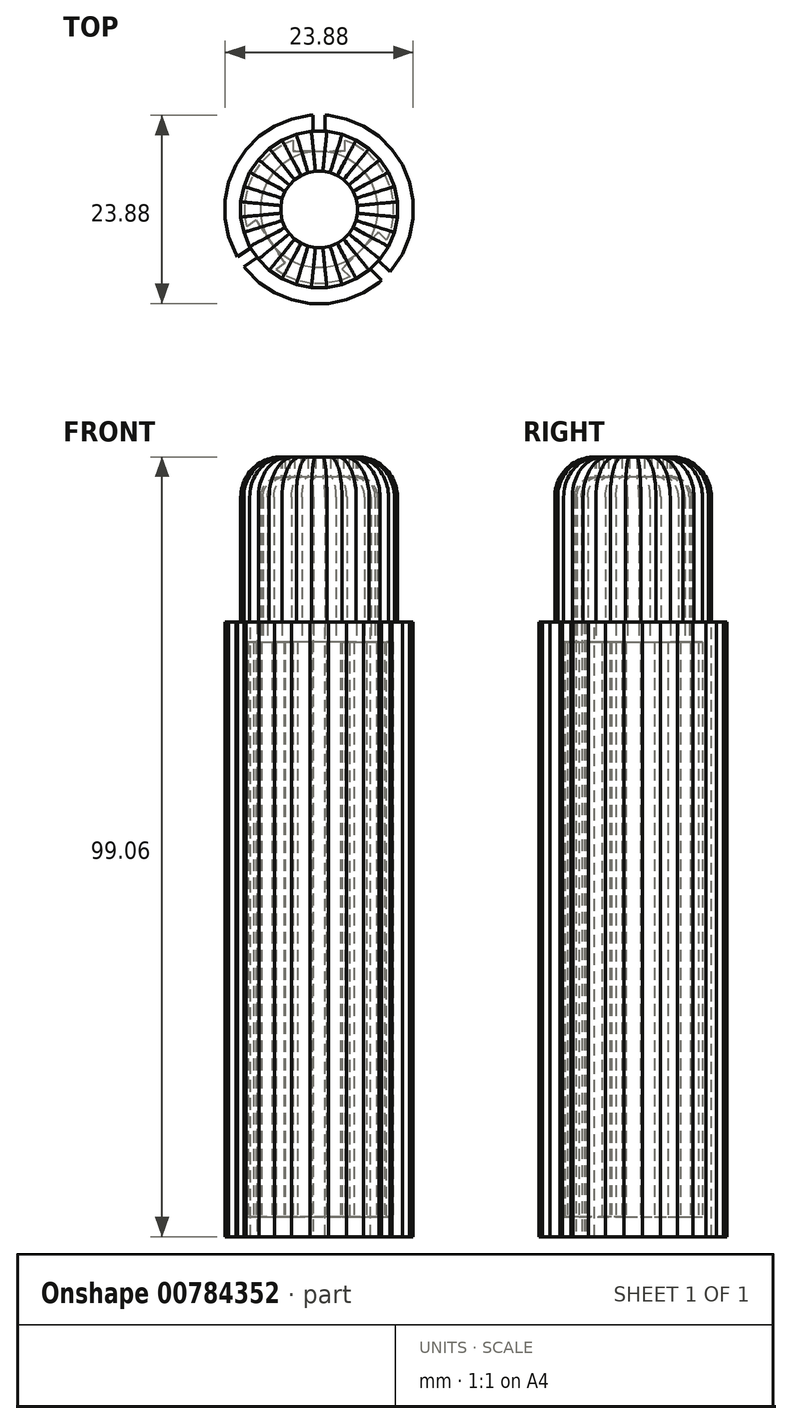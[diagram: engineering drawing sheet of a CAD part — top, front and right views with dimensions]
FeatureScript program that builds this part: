
annotation { "Feature Type Name" : "Feature", "Feature Type Description" : "" }
export const myFeature = defineFeature(function(context is Context, id is Id, definition is map)
    precondition{}
    {
        {
            var Q0;
            Q0=qCreatedBy(makeId("Top.planeOp"),FACE);
            var sketch = newSketch(context, id + "F0", { "sketchPlane" : qUnion([Q0])});
            skCircle(sketch, "E0.cCircle", {"center": v(0, 0) * mm, "radius": 9.95 * mm, "construction": true});
            skLineSegment(sketch, "E0.0", {"start": v(-0.98, 9.95) * mm, "end": v(-0.67, 9.95) * mm});
            skLineSegment(sketch, "E0.1", {"start": v(0.98, 9.95) * mm, "end": v(2.9, 9.57) * mm});
            skLineSegment(sketch, "E0.2", {"start": v(2.9, 9.57) * mm, "end": v(4.71, 8.82) * mm});
            skLineSegment(sketch, "E0.3", {"start": v(4.71, 8.82) * mm, "end": v(6.34, 7.73) * mm});
            skLineSegment(sketch, "E0.4", {"start": v(6.34, 7.73) * mm, "end": v(7.73, 6.34) * mm});
            skLineSegment(sketch, "E0.5", {"start": v(7.73, 6.34) * mm, "end": v(8.82, 4.71) * mm});
            skLineSegment(sketch, "E0.6", {"start": v(8.82, 4.71) * mm, "end": v(9.57, 2.9) * mm});
            skLineSegment(sketch, "E0.7", {"start": v(9.57, 2.9) * mm, "end": v(9.95, 0.98) * mm});
            skLineSegment(sketch, "E0.8", {"start": v(9.95, 0.98) * mm, "end": v(9.95, -0.98) * mm});
            skLineSegment(sketch, "E0.9", {"start": v(9.95, -0.98) * mm, "end": v(9.57, -2.9) * mm});
            skLineSegment(sketch, "E0.10", {"start": v(9.57, -2.9) * mm, "end": v(8.82, -4.71) * mm});
            skLineSegment(sketch, "E0.11", {"start": v(8.82, -4.71) * mm, "end": v(7.73, -6.34) * mm});
            skLineSegment(sketch, "E0.12", {"start": v(7.73, -6.34) * mm, "end": v(6.34, -7.73) * mm});
            skLineSegment(sketch, "E0.13", {"start": v(6.34, -7.73) * mm, "end": v(6.15, -7.86) * mm});
            skLineSegment(sketch, "E0.14", {"start": v(4.71, -8.82) * mm, "end": v(2.9, -9.57) * mm});
            skLineSegment(sketch, "E0.15", {"start": v(2.9, -9.57) * mm, "end": v(0.98, -9.95) * mm});
            skLineSegment(sketch, "E0.16", {"start": v(0.98, -9.95) * mm, "end": v(-0.98, -9.95) * mm});
            skLineSegment(sketch, "E0.17", {"start": v(-0.98, -9.95) * mm, "end": v(-2.9, -9.57) * mm});
            skLineSegment(sketch, "E0.18", {"start": v(-2.9, -9.57) * mm, "end": v(-4.71, -8.82) * mm});
            skLineSegment(sketch, "E0.19", {"start": v(-4.71, -8.82) * mm, "end": v(-6.34, -7.73) * mm});
            skLineSegment(sketch, "E0.20", {"start": v(-6.34, -7.73) * mm, "end": v(-7.73, -6.34) * mm});
            skLineSegment(sketch, "E0.21", {"start": v(-7.73, -6.34) * mm, "end": v(-7.86, -6.15) * mm});
            skLineSegment(sketch, "E0.22", {"start": v(-8.82, -4.71) * mm, "end": v(-9.57, -2.9) * mm});
            skLineSegment(sketch, "E0.23", {"start": v(-9.57, -2.9) * mm, "end": v(-9.95, -0.98) * mm});
            skLineSegment(sketch, "E0.24", {"start": v(-9.95, -0.98) * mm, "end": v(-9.95, 0.98) * mm});
            skLineSegment(sketch, "E0.25", {"start": v(-9.95, 0.98) * mm, "end": v(-9.57, 2.9) * mm});
            skLineSegment(sketch, "E0.26", {"start": v(-9.57, 2.9) * mm, "end": v(-8.82, 4.71) * mm});
            skLineSegment(sketch, "E0.27", {"start": v(-8.82, 4.71) * mm, "end": v(-7.73, 6.34) * mm});
            skLineSegment(sketch, "E0.28", {"start": v(-7.73, 6.34) * mm, "end": v(-6.34, 7.73) * mm});
            skLineSegment(sketch, "E0.29", {"start": v(-6.34, 7.73) * mm, "end": v(-4.71, 8.82) * mm});
            skLineSegment(sketch, "E0.30", {"start": v(-4.71, 8.82) * mm, "end": v(-2.9, 9.57) * mm});
            skLineSegment(sketch, "E0.31", {"start": v(-2.9, 9.57) * mm, "end": v(-0.98, 9.95) * mm});
            skPoint(sketch, "E0.0.midPoint", {"position": v(0, 9.95) * mm});
            skLineSegment(sketch, "E1.trimOffspring", {"start": v(0.82, 9.95) * mm, "end": v(0.98, 9.95) * mm});
            skLineSegment(sketch, "E2.trimOffspring", {"start": v(-8.7, -4.9) * mm, "end": v(-8.82, -4.71) * mm});
            skPoint(sketch, "E3.orphan", {"position": v(-8.27, -5.53) * mm});
            skPoint(sketch, "E4.start.orphan", {"position": v(5.53, -8.27) * mm});
            skLineSegment(sketch, "E5.trimOffspring", {"start": v(4.9, -8.7) * mm, "end": v(4.71, -8.82) * mm});
            skLineSegment(sketch, "E6", {"start": v(-0.67, 9.95) * mm, "end": v(0.82, 9.95) * mm});
            skLineSegment(sketch, "E7", {"start": v(6.15, -7.86) * mm, "end": v(4.9, -8.7) * mm});
            skLineSegment(sketch, "E8", {"start": v(-8.7, -4.9) * mm, "end": v(-7.86, -6.15) * mm});
            skSolve(sketch);
        }
        {
            var Q0;
            Q0=qCreatedBy(makeId("Top.planeOp"),FACE);
            var sketch = newSketch(context, id + "F1", { "sketchPlane" : qUnion([Q0])});
            skCircle(sketch, "E9.cCircle", {"center": v(0, 0) * mm, "radius": 11.94 * mm, "construction": true});
            skLineSegment(sketch, "E9.0", {"start": v(-1.18, 11.94) * mm, "end": v(-0.75, 11.94) * mm});
            skLineSegment(sketch, "E9.1", {"start": v(1.18, 11.94) * mm, "end": v(3.48, 11.48) * mm});
            skLineSegment(sketch, "E9.2", {"start": v(3.48, 11.48) * mm, "end": v(5.66, 10.58) * mm});
            skLineSegment(sketch, "E9.3", {"start": v(5.66, 10.58) * mm, "end": v(7.61, 9.28) * mm});
            skLineSegment(sketch, "E9.4", {"start": v(7.61, 9.28) * mm, "end": v(9.28, 7.61) * mm});
            skLineSegment(sketch, "E9.5", {"start": v(9.28, 7.61) * mm, "end": v(10.58, 5.66) * mm});
            skLineSegment(sketch, "E9.6", {"start": v(10.58, 5.66) * mm, "end": v(11.48, 3.48) * mm});
            skLineSegment(sketch, "E9.7", {"start": v(11.48, 3.48) * mm, "end": v(11.94, 1.18) * mm});
            skLineSegment(sketch, "E9.8", {"start": v(11.94, 1.18) * mm, "end": v(11.94, -1.18) * mm});
            skLineSegment(sketch, "E9.9", {"start": v(11.94, -1.18) * mm, "end": v(11.48, -3.48) * mm});
            skLineSegment(sketch, "E9.10", {"start": v(11.48, -3.48) * mm, "end": v(10.58, -5.66) * mm});
            skLineSegment(sketch, "E9.11", {"start": v(10.58, -5.66) * mm, "end": v(9.28, -7.61) * mm});
            skLineSegment(sketch, "E9.12", {"start": v(9.28, -7.61) * mm, "end": v(8.97, -7.91) * mm});
            skLineSegment(sketch, "E9.13", {"start": v(7.61, -9.28) * mm, "end": v(5.66, -10.58) * mm});
            skLineSegment(sketch, "E9.14", {"start": v(5.66, -10.58) * mm, "end": v(3.48, -11.48) * mm});
            skLineSegment(sketch, "E9.15", {"start": v(3.48, -11.48) * mm, "end": v(1.18, -11.94) * mm});
            skLineSegment(sketch, "E9.16", {"start": v(1.18, -11.94) * mm, "end": v(-1.18, -11.94) * mm});
            skLineSegment(sketch, "E9.17", {"start": v(-1.18, -11.94) * mm, "end": v(-3.48, -11.48) * mm});
            skLineSegment(sketch, "E9.18", {"start": v(-3.48, -11.48) * mm, "end": v(-5.66, -10.58) * mm});
            skLineSegment(sketch, "E9.19", {"start": v(-5.66, -10.58) * mm, "end": v(-7.61, -9.28) * mm});
            skLineSegment(sketch, "E9.20", {"start": v(-7.61, -9.28) * mm, "end": v(-9.28, -7.61) * mm});
            skLineSegment(sketch, "E9.21", {"start": v(-9.28, -7.61) * mm, "end": v(-9.51, -7.26) * mm});
            skLineSegment(sketch, "E9.22", {"start": v(-10.58, -5.66) * mm, "end": v(-11.48, -3.48) * mm});
            skLineSegment(sketch, "E9.23", {"start": v(-11.48, -3.48) * mm, "end": v(-11.94, -1.18) * mm});
            skLineSegment(sketch, "E9.24", {"start": v(-11.94, -1.18) * mm, "end": v(-11.94, 1.18) * mm});
            skLineSegment(sketch, "E9.25", {"start": v(-11.94, 1.18) * mm, "end": v(-11.48, 3.48) * mm});
            skLineSegment(sketch, "E9.26", {"start": v(-11.48, 3.48) * mm, "end": v(-10.58, 5.66) * mm});
            skLineSegment(sketch, "E9.27", {"start": v(-10.58, 5.66) * mm, "end": v(-9.28, 7.61) * mm});
            skLineSegment(sketch, "E9.28", {"start": v(-9.28, 7.61) * mm, "end": v(-7.61, 9.28) * mm});
            skLineSegment(sketch, "E9.29", {"start": v(-7.61, 9.28) * mm, "end": v(-5.66, 10.58) * mm});
            skLineSegment(sketch, "E9.30", {"start": v(-5.66, 10.58) * mm, "end": v(-3.48, 11.48) * mm});
            skLineSegment(sketch, "E9.31", {"start": v(-3.48, 11.48) * mm, "end": v(-1.18, 11.94) * mm});
            skPoint(sketch, "E9.0.midPoint", {"position": v(0, 11.94) * mm});
            skLineSegment(sketch, "E10", {"start": v(-0.75, 11.94) * mm, "end": v(-0.75, 9.94) * mm});
            skLineSegment(sketch, "E11", {"start": v(-0.75, 9.94) * mm, "end": v(0.75, 9.94) * mm});
            skLineSegment(sketch, "E12", {"start": v(0.75, 9.94) * mm, "end": v(0.75, 11.94) * mm});
            skLineSegment(sketch, "E13.trimOffspring", {"start": v(0.75, 11.94) * mm, "end": v(1.18, 11.94) * mm});
            skLineSegment(sketch, "E14", {"start": v(7.03, -7.03) * mm, "end": v(7.56, -6.5) * mm});
            skLineSegment(sketch, "E15", {"start": v(7.03, -7.03) * mm, "end": v(6.5, -7.56) * mm});
            skLineSegment(sketch, "E16", {"start": v(6.5, -7.56) * mm, "end": v(7.91, -8.97) * mm});
            skLineSegment(sketch, "E17", {"start": v(7.56, -6.5) * mm, "end": v(8.97, -7.91) * mm});
            skLineSegment(sketch, "E18.trimOffspring", {"start": v(7.91, -8.97) * mm, "end": v(7.61, -9.28) * mm});
            skPoint(sketch, "E19.start.orphan", {"position": v(8.44, -8.44) * mm});
            skLineSegment(sketch, "E20", {"start": v(-8.27, -5.52) * mm, "end": v(-8.68, -4.9) * mm});
            skLineSegment(sketch, "E21", {"start": v(-8.27, -5.52) * mm, "end": v(-7.85, -6.15) * mm});
            skLineSegment(sketch, "E22", {"start": v(-7.85, -6.15) * mm, "end": v(-9.51, -7.26) * mm});
            skLineSegment(sketch, "E23", {"start": v(-8.68, -4.9) * mm, "end": v(-10.35, -6.01) * mm});
            skPoint(sketch, "E24.start.orphan", {"position": v(-9.93, -6.63) * mm});
            skLineSegment(sketch, "E25.trimOffspring", {"start": v(-10.35, -6.01) * mm, "end": v(-10.58, -5.66) * mm});
            skSolve(sketch);
        }
        {
            var Q0;
            Q0=makeQuery(id+"F0.imprint","IMPRINT",FACE,{"disambiguationData":[TD([[makeQuery(id+"F0.imprint","IMPRINT",EDGE,{"derivedFrom":sQuery(id+"F0.wireOp",EDGE,"E0.0")}),-1.0]])]});
            extrude(context, id + "F2", {"entities" : qUnion([Q0]), "depth" : 90 * mm, "offsetDistance" : 25.4 * mm});
        }
        {
            var Q0;
            Q0=makeQuery(id+"F1.imprint","IMPRINT",FACE,{"disambiguationData":[TD([[makeQuery(id+"F1.imprint","IMPRINT",EDGE,{"derivedFrom":sQuery(id+"F1.wireOp",EDGE,"E9.0")}),-1.0]])]});
            extrude(context, id + "F3", {"entities" : qUnion([Q0]), "operationType" : NewBodyOperationType.ADD, "depth" : 78.08 * mm, "offsetDistance" : 25.4 * mm});
        }
        {
            var Q0;
            Q0 = qSketchRegion(id + "F0", true);
            extrude(context, id + "F4", {"entities" : qUnion([Q0]), "operationType" : NewBodyOperationType.ADD, "depth" : 99.06 * mm, "offsetDistance" : 25.4 * mm});
        }
        {
            var Q0;
            Q0=makeQuery(id+"F4.opExtrude","CAP_EDGE",EDGE,{"disambiguationData":[OSD([sQuery(id+"F0.wireOp",EDGE,"E0.26")])],"isStart":false});
            var Q1;
            Q1=makeQuery(id+"F4.opExtrude","CAP_EDGE",EDGE,{"disambiguationData":[OSD([sQuery(id+"F0.wireOp",EDGE,"E0.23")])],"isStart":false});
            var Q2;
            Q2=makeQuery(id+"F4.opExtrude","CAP_EDGE",EDGE,{"disambiguationData":[OSD([sQuery(id+"F0.wireOp",EDGE,"E0.24")])],"isStart":false});
            var Q3;
            Q3=makeQuery(id+"F4.opExtrude","CAP_EDGE",EDGE,{"disambiguationData":[OSD([sQuery(id+"F0.wireOp",EDGE,"E0.25")])],"isStart":false});
            var Q4;
            Q4=makeQuery(id+"F4.opExtrude","CAP_EDGE",EDGE,{"disambiguationData":[OSD([sQuery(id+"F0.wireOp",EDGE,"E0.22")])],"isStart":false});
            var Q5;
            Q5=makeQuery(id+"F4.opExtrude","CAP_EDGE",EDGE,{"disambiguationData":[OSD([sQuery(id+"F0.wireOp",EDGE,"E0.21"),sQuery(id+"F0.wireOp",EDGE,"E2.trimOffspring"),sQuery(id+"F0.wireOp",EDGE,"E8")])],"isStart":false});
            var Q6;
            Q6=makeQuery(id+"F4.opExtrude","CAP_EDGE",EDGE,{"disambiguationData":[OSD([sQuery(id+"F0.wireOp",EDGE,"E0.20")])],"isStart":false});
            var Q7;
            Q7=makeQuery(id+"F4.opExtrude","CAP_EDGE",EDGE,{"disambiguationData":[OSD([sQuery(id+"F0.wireOp",EDGE,"E0.19")])],"isStart":false});
            var Q8;
            Q8=makeQuery(id+"F4.opExtrude","CAP_EDGE",EDGE,{"disambiguationData":[OSD([sQuery(id+"F0.wireOp",EDGE,"E0.18")])],"isStart":false});
            var Q9;
            Q9=makeQuery(id+"F4.opExtrude","CAP_EDGE",EDGE,{"disambiguationData":[OSD([sQuery(id+"F0.wireOp",EDGE,"E0.17")])],"isStart":false});
            var Q10;
            Q10=makeQuery(id+"F4.opExtrude","CAP_EDGE",EDGE,{"disambiguationData":[OSD([sQuery(id+"F0.wireOp",EDGE,"E0.27")])],"isStart":false});
            var Q11;
            Q11=makeQuery(id+"F4.opExtrude","CAP_EDGE",EDGE,{"disambiguationData":[OSD([sQuery(id+"F0.wireOp",EDGE,"E0.28")])],"isStart":false});
            var Q12;
            Q12=makeQuery(id+"F4.opExtrude","CAP_EDGE",EDGE,{"disambiguationData":[OSD([sQuery(id+"F0.wireOp",EDGE,"E0.29")])],"isStart":false});
            var Q13;
            Q13=makeQuery(id+"F4.opExtrude","CAP_EDGE",EDGE,{"disambiguationData":[OSD([sQuery(id+"F0.wireOp",EDGE,"E0.16")])],"isStart":false});
            var Q14;
            Q14=makeQuery(id+"F4.opExtrude","CAP_EDGE",EDGE,{"disambiguationData":[OSD([sQuery(id+"F0.wireOp",EDGE,"E0.15")])],"isStart":false});
            var Q15;
            Q15=makeQuery(id+"F4.opExtrude","CAP_EDGE",EDGE,{"disambiguationData":[OSD([sQuery(id+"F0.wireOp",EDGE,"E0.14")])],"isStart":false});
            var Q16;
            Q16=makeQuery(id+"F4.opExtrude","CAP_EDGE",EDGE,{"disambiguationData":[OSD([sQuery(id+"F0.wireOp",EDGE,"E0.13"),sQuery(id+"F0.wireOp",EDGE,"E5.trimOffspring"),sQuery(id+"F0.wireOp",EDGE,"E7")])],"isStart":false});
            var Q17;
            Q17=makeQuery(id+"F4.opExtrude","CAP_EDGE",EDGE,{"disambiguationData":[OSD([sQuery(id+"F0.wireOp",EDGE,"E0.12")])],"isStart":false});
            var Q18;
            Q18=makeQuery(id+"F4.opExtrude","CAP_EDGE",EDGE,{"disambiguationData":[OSD([sQuery(id+"F0.wireOp",EDGE,"E0.11")])],"isStart":false});
            var Q19;
            Q19=makeQuery(id+"F4.opExtrude","CAP_EDGE",EDGE,{"disambiguationData":[OSD([sQuery(id+"F0.wireOp",EDGE,"E0.10")])],"isStart":false});
            var Q20;
            Q20=makeQuery(id+"F4.opExtrude","CAP_EDGE",EDGE,{"disambiguationData":[OSD([sQuery(id+"F0.wireOp",EDGE,"E0.9")])],"isStart":false});
            var Q21;
            Q21=makeQuery(id+"F4.opExtrude","CAP_EDGE",EDGE,{"disambiguationData":[OSD([sQuery(id+"F0.wireOp",EDGE,"E0.8")])],"isStart":false});
            var Q22;
            Q22=makeQuery(id+"F4.opExtrude","CAP_EDGE",EDGE,{"disambiguationData":[OSD([sQuery(id+"F0.wireOp",EDGE,"E0.7")])],"isStart":false});
            var Q23;
            Q23=makeQuery(id+"F4.opExtrude","CAP_EDGE",EDGE,{"disambiguationData":[OSD([sQuery(id+"F0.wireOp",EDGE,"E0.6")])],"isStart":false});
            var Q24;
            Q24=makeQuery(id+"F4.opExtrude","CAP_EDGE",EDGE,{"disambiguationData":[OSD([sQuery(id+"F0.wireOp",EDGE,"E0.5")])],"isStart":false});
            var Q25;
            Q25=makeQuery(id+"F4.opExtrude","CAP_EDGE",EDGE,{"disambiguationData":[OSD([sQuery(id+"F0.wireOp",EDGE,"E0.3")])],"isStart":false});
            var Q26;
            Q26=makeQuery(id+"F4.opExtrude","CAP_EDGE",EDGE,{"disambiguationData":[OSD([sQuery(id+"F0.wireOp",EDGE,"E0.2")])],"isStart":false});
            var Q27;
            Q27=makeQuery(id+"F4.opExtrude","CAP_EDGE",EDGE,{"disambiguationData":[OSD([sQuery(id+"F0.wireOp",EDGE,"E0.30")])],"isStart":false});
            var Q28;
            Q28=makeQuery(id+"F4.opExtrude","CAP_EDGE",EDGE,{"disambiguationData":[OSD([sQuery(id+"F0.wireOp",EDGE,"E0.31")])],"isStart":false});
            var Q29;
            Q29=makeQuery(id+"F4.opExtrude","CAP_EDGE",EDGE,{"disambiguationData":[OSD([sQuery(id+"F0.wireOp",EDGE,"E0.1")])],"isStart":false});
            var Q30;
            Q30=makeQuery(id+"F4.opExtrude","CAP_EDGE",EDGE,{"disambiguationData":[OSD([sQuery(id+"F0.wireOp",EDGE,"E0.0"),sQuery(id+"F0.wireOp",EDGE,"E1.trimOffspring"),sQuery(id+"F0.wireOp",EDGE,"E6")])],"isStart":false});
            var Q31;
            Q31=makeQuery(id+"F4.opExtrude","CAP_EDGE",EDGE,{"disambiguationData":[OSD([sQuery(id+"F0.wireOp",EDGE,"E0.4")])],"isStart":false});
            fillet(context, id + "F5", {"entities" : qUnion([Q0, Q1, Q2, Q3, Q4, Q5, Q6, Q7, Q8, Q9, Q10, Q11, Q12, Q13, Q14, Q15, Q16, Q17, Q18, Q19, Q20, Q21, Q22, Q23, Q24, Q25, Q26, Q27, Q28, Q29, Q30, Q31]), "radius" : 5.08 * mm, "tangentPropagation" : true, "allowEdgeOverflow" : false});
        }
        {
            var Q0;
            Q0=makeQuery(id+"F4.opExtrude","CAP_FACE",FACE,{"disambiguationData":[OSD([sQuery(id+"F0.wireOp",EDGE,"E0.0"),sQuery(id+"F0.wireOp",EDGE,"E0.1"),sQuery(id+"F0.wireOp",EDGE,"E0.2"),sQuery(id+"F0.wireOp",EDGE,"E0.3"),sQuery(id+"F0.wireOp",EDGE,"E0.4"),sQuery(id+"F0.wireOp",EDGE,"E0.5"),sQuery(id+"F0.wireOp",EDGE,"E0.6"),sQuery(id+"F0.wireOp",EDGE,"E0.7"),sQuery(id+"F0.wireOp",EDGE,"E0.8"),sQuery(id+"F0.wireOp",EDGE,"E0.9"),sQuery(id+"F0.wireOp",EDGE,"E0.10"),sQuery(id+"F0.wireOp",EDGE,"E0.11"),sQuery(id+"F0.wireOp",EDGE,"E0.12"),sQuery(id+"F0.wireOp",EDGE,"E0.13"),sQuery(id+"F0.wireOp",EDGE,"E0.14"),sQuery(id+"F0.wireOp",EDGE,"E0.15"),sQuery(id+"F0.wireOp",EDGE,"E0.16"),sQuery(id+"F0.wireOp",EDGE,"E0.17"),sQuery(id+"F0.wireOp",EDGE,"E0.18"),sQuery(id+"F0.wireOp",EDGE,"E0.19"),sQuery(id+"F0.wireOp",EDGE,"E0.20"),sQuery(id+"F0.wireOp",EDGE,"E0.21"),sQuery(id+"F0.wireOp",EDGE,"E0.22"),sQuery(id+"F0.wireOp",EDGE,"E0.23"),sQuery(id+"F0.wireOp",EDGE,"E0.24"),sQuery(id+"F0.wireOp",EDGE,"E0.25"),sQuery(id+"F0.wireOp",EDGE,"E0.26"),sQuery(id+"F0.wireOp",EDGE,"E0.27"),sQuery(id+"F0.wireOp",EDGE,"E0.28"),sQuery(id+"F0.wireOp",EDGE,"E0.29"),sQuery(id+"F0.wireOp",EDGE,"E0.30"),sQuery(id+"F0.wireOp",EDGE,"E0.31"),sQuery(id+"F0.wireOp",EDGE,"E1.trimOffspring"),sQuery(id+"F0.wireOp",EDGE,"E2.trimOffspring"),sQuery(id+"F0.wireOp",EDGE,"E5.trimOffspring"),sQuery(id+"F0.wireOp",EDGE,"E6"),sQuery(id+"F0.wireOp",EDGE,"E7"),sQuery(id+"F0.wireOp",EDGE,"E8")])],"isStart":false});
            shell(context, id + "F6", {"entities" : qUnion([Q0]), "thickness" : 2.54 * mm});
        }
    });
